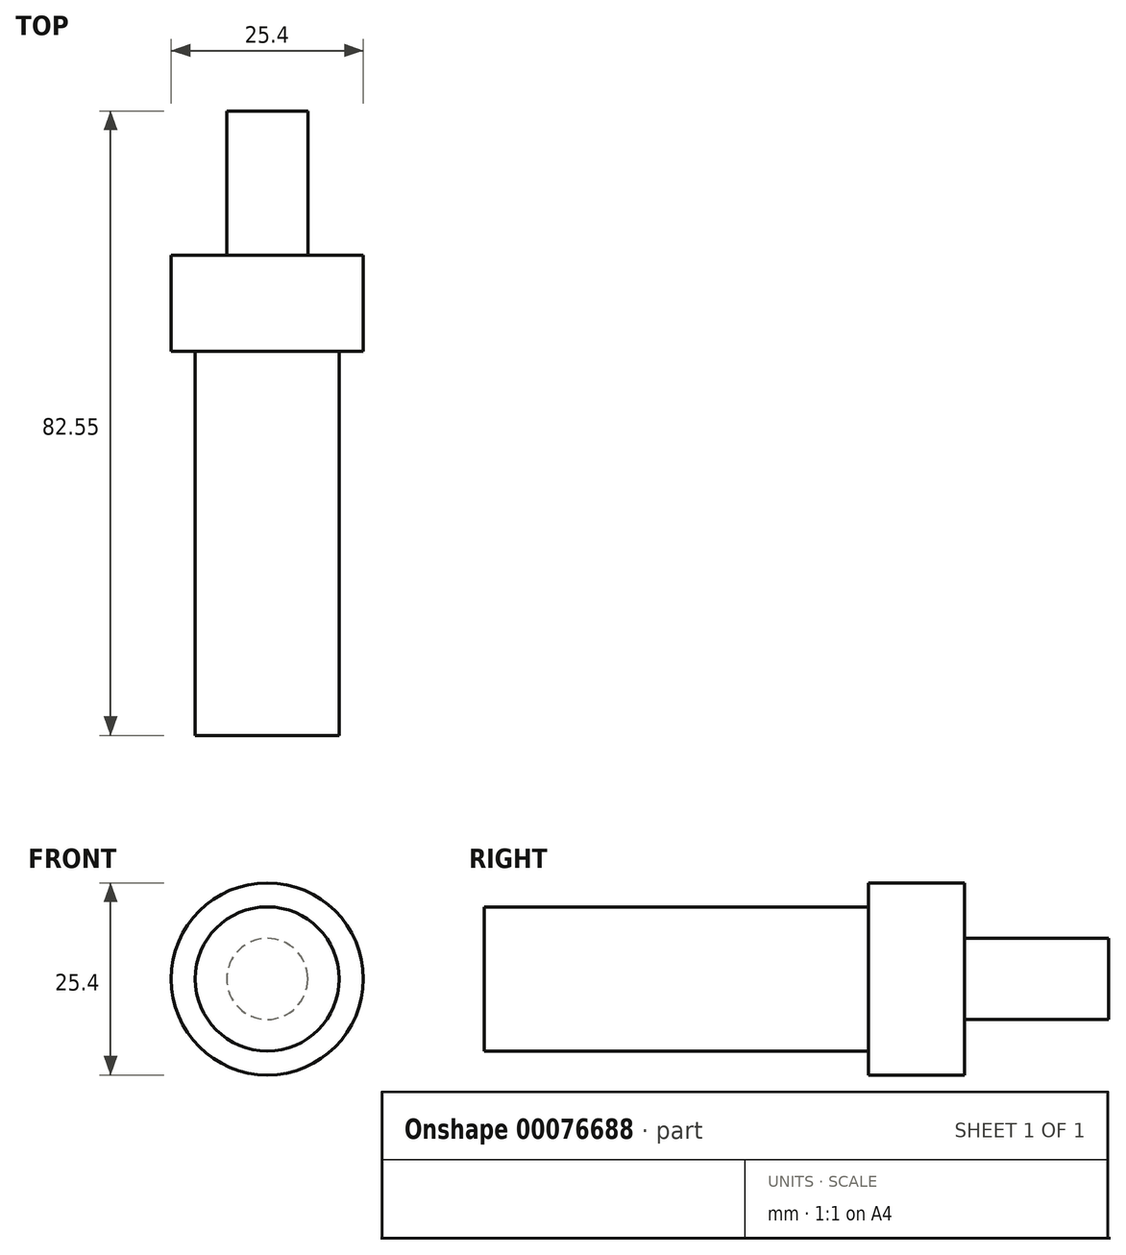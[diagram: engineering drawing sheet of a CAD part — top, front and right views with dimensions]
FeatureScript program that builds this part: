
annotation { "Feature Type Name" : "Feature", "Feature Type Description" : "" }
export const myFeature = defineFeature(function(context is Context, id is Id, definition is map)
    precondition{}
    {
        {
            var Q0;
            Q0=qCreatedBy(makeId("Front.planeOp"),FACE);
            var sketch = newSketch(context, id + "F0", { "sketchPlane" : qUnion([Q0])});
            skCircle(sketch, "E0", {"center": v(0, 0) * mm, "radius": 12.7 * mm});
            skCircle(sketch, "E1", {"center": v(0, 0) * mm, "radius": 5.36 * mm});
            skSolve(sketch);
        }
        {
            var Q0;
            Q0=makeQuery(id+"F0.imprint","IMPRINT",FACE,{"disambiguationData":[TD([[makeQuery(id+"F0.imprint","IMPRINT",EDGE,{"derivedFrom":sQuery(id+"F0.wireOp",EDGE,"E0")}),1.0]])]});
            var Q1;
            Q1=makeQuery(id+"F0.imprint","IMPRINT",FACE,{"disambiguationData":[TD([[makeQuery(id+"F0.imprint","IMPRINT",EDGE,{"derivedFrom":sQuery(id+"F0.wireOp",EDGE,"E1")}),1.0]])]});
            extrude(context, id + "F1", {"entities" : qUnion([Q0, Q1]), "depth" : 12.7 * mm});
        }
        {
            var Q0;
            Q0=makeQuery(id+"F0.imprint","IMPRINT",FACE,{"disambiguationData":[TD([[makeQuery(id+"F0.imprint","IMPRINT",EDGE,{"derivedFrom":sQuery(id+"F0.wireOp",EDGE,"E1")}),1.0]])]});
            extrude(context, id + "F2", {"entities" : qUnion([Q0]), "operationType" : NewBodyOperationType.ADD, "oppositeDirection" : true, "depth" : 19.05 * mm});
        }
        {
            var Q0;
            Q0=makeQuery(id+"F1.opExtrude","CAP_FACE",FACE,{"disambiguationData":[OSD([sQuery(id+"F0.wireOp",EDGE,"E0")])],"isStart":false});
            var sketch = newSketch(context, id + "F3", { "sketchPlane" : qUnion([Q0])});
            skCircle(sketch, "E2", {"center": v(0, 0) * mm, "radius": 9.53 * mm});
            skSolve(sketch);
        }
        {
            var Q0;
            Q0=makeQuery(id+"F3.imprint","IMPRINT",FACE,{"disambiguationData":[TD([[makeQuery(id+"F3.imprint","IMPRINT",EDGE,{"derivedFrom":sQuery(id+"F3.wireOp",EDGE,"E2")}),1.0]])]});
            extrude(context, id + "F4", {"entities" : qUnion([Q0]), "operationType" : NewBodyOperationType.ADD, "depth" : 50.8 * mm});
        }
    });
